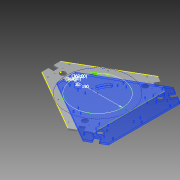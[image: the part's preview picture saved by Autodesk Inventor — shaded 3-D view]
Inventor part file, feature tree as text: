
AUTODESK INVENTOR PART (.ipt)
format: ipt  version: 2015 SP1 (Build 190203100, 203)  size: 232,448 bytes
history: native  units: mm
features: sketch x5, reference x5, extrude x4, hole x3
ambient origin geometry x8: Origin, YZ Plane, XZ Plane, XY Plane, X Axis, Y Axis, Z Axis, Center Point
bodies: Solid1 (feature_tree)
feature tree (17):
  extrude  "Extrusion1"  Depth=6.35mm TaperAngle=0.0deg
  hole  "Hole1"  [1 undecoded]
  extrude  "Extrusion2"  Depth=31.0mm
  hole  "Hole2"  [1 undecoded]
  sketch  "Sketch5"  dims[d17=3.4mm d18=6.0mm d19=6.5mm d20=3.0mm d21=90.0deg d22=8.0mm d23=20.594885mm d24=22.5mm d25=30.0mm d27=360.0deg d29=0.0mm d30=0.0mm d31=20.0mm d32=20.0mm d33=30.0mm d35=360.0deg d37=4.5mm d38=6.0mm d39=8.0mm d40=4.0mm d41=90.0deg d42=8.0mm d43=20.594885mm d45=190.0mm d46=25.0mm d47=60.0mm d49=360.0deg d51=10.0mm d52=0.0mm d53=3.4mm d54=6.0mm d55=6.5mm d56=3.0mm d57=90.0deg d58=8.0mm d59=20.594885mm d60=10.0mm d61=60.0mm d63=360.0deg d65=10.0mm d66=0.0mm]
  extrude  "Extrusion3"  Depth=10.0mm
  hole  "Hole3"  [1 undecoded]
  extrude  "Extrusion4"  TaperAngle=0.0deg  [1 undecoded]
  sketch  "Sketch1"  dims[d0=20.0mm d1=20.0mm d2=20.0mm d3=20.0mm d4=20.0mm d5=20.0mm d6=6.35mm d7=0.0mm]
  sketch  "Sketch2"  dims[d8=180.0mm d9=42.5mm]
  reference  "Reference1"
  reference  "Reference2"
  reference  "Reference3"
  sketch  "Sketch3"  dims[d10=42.5mm d11=31.0mm]
  sketch  "Sketch4"  dims[d12=31.0mm d13=30.0mm d15=360.0deg]
  reference  "Reference4"
  reference  "Reference5"
note: 4 required parameter values undecoded (feature->parameter linkage not recoverable at this tier; creation-order binding heuristic only, values carry confidence <= 0.55)
